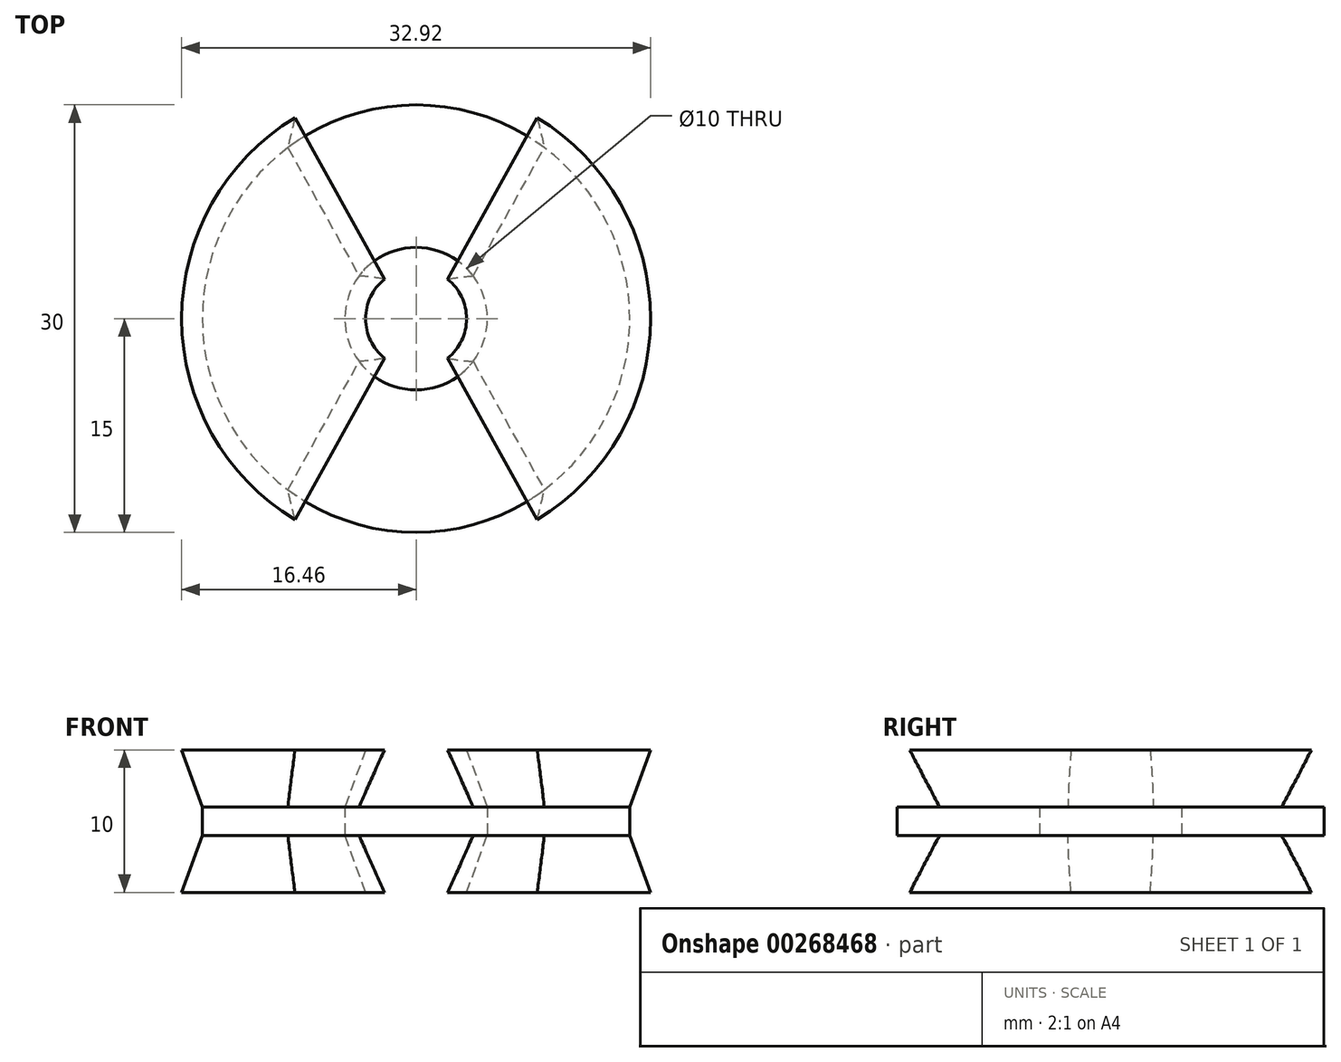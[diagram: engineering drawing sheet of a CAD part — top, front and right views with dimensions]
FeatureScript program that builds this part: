
annotation { "Feature Type Name" : "Feature", "Feature Type Description" : "" }
export const myFeature = defineFeature(function(context is Context, id is Id, definition is map)
    precondition{}
    {
        {
            var Q0;
            Q0=qCreatedBy(makeId("Top.planeOp"),FACE);
            var sketch = newSketch(context, id + "F0", { "sketchPlane" : qUnion([Q0])});
            skCircle(sketch, "E0", {"center": v(0, 0) * mm, "radius": 15 * mm});
            skCircle(sketch, "E1", {"center": v(0, 0) * mm, "radius": 5 * mm});
            skSolve(sketch);
        }
        {
            var Q0;
            Q0=makeQuery(id+"F0.imprint","IMPRINT",FACE,{"disambiguationData":[TD([[makeQuery(id+"F0.imprint","IMPRINT",EDGE,{"derivedFrom":sQuery(id+"F0.wireOp",EDGE,"E0")}),1.0]])]});
            extrude(context, id + "F1", {"entities" : qUnion([Q0]), "depth" : 2 * mm});
        }
        {
            var Q0;
            Q0=makeQuery(id+"F1.opExtrude","CAP_FACE",FACE,{"disambiguationData":[OSD([sQuery(id+"F0.wireOp",EDGE,"E0"),sQuery(id+"F0.wireOp",EDGE,"E1")])],"isStart":false});
            var sketch = newSketch(context, id + "F2", { "sketchPlane" : qUnion([Q0])});
            skLineSegment(sketch, "E2", {"start": v(-4, 3) * mm, "end": v(-9, 12) * mm});
            skLineSegment(sketch, "E3", {"start": v(4, 3) * mm, "end": v(9, 12) * mm});
            skLineSegment(sketch, "E4", {"start": v(4, -3) * mm, "end": v(9, -12) * mm});
            skLineSegment(sketch, "E5", {"start": v(-4, -3) * mm, "end": v(-9, -12) * mm});
            skSolve(sketch);
        }
        {
            var Q0;
            {var subQ0=sQuery(id+"F2.wireOp",EDGE,"E2");Q0=makeQuery(id+"F2.imprint","IMPRINT",FACE,{"disambiguationData":[TD([[makeQuery(id+"F2.imprint","IMPRINT",EDGE,{"derivedFrom":subQ0}),1.0]])]});}
            var Q1;
            {var subQ0=sQuery(id+"F2.wireOp",EDGE,"E3");Q1=makeQuery(id+"F2.imprint","IMPRINT",FACE,{"disambiguationData":[TD([[makeQuery(id+"F2.imprint","IMPRINT",EDGE,{"derivedFrom":subQ0}),-1.0]])]});}
            extrude(context, id + "F3", {"entities" : qUnion([Q0, Q1]), "operationType" : NewBodyOperationType.ADD, "depth" : 4 * mm, "hasDraft" : true, "draftAngle" : 20 * degree});
        }
        {
            var Q0;
            Q0=makeQuery(id+"F1.opExtrude","CAP_FACE",FACE,{"disambiguationData":[OSD([sQuery(id+"F0.wireOp",EDGE,"E0"),sQuery(id+"F0.wireOp",EDGE,"E1")])],"isStart":true});
            var sketch = newSketch(context, id + "F4", { "sketchPlane" : qUnion([Q0])});
            skLineSegment(sketch, "E6", {"start": v(-4, 3) * mm, "end": v(-9, 12) * mm});
            skLineSegment(sketch, "E7", {"start": v(4, 3) * mm, "end": v(9, 12) * mm});
            skLineSegment(sketch, "E8", {"start": v(9, -12) * mm, "end": v(4, -3) * mm});
            skLineSegment(sketch, "E9", {"start": v(-4, -3) * mm, "end": v(-9, -12) * mm});
            skSolve(sketch);
        }
        {
            var Q0;
            {var subQ0=sQuery(id+"F4.wireOp",EDGE,"E6");Q0=makeQuery(id+"F4.imprint","IMPRINT",FACE,{"disambiguationData":[TD([[makeQuery(id+"F4.imprint","IMPRINT",EDGE,{"derivedFrom":subQ0}),1.0]])]});}
            var Q1;
            {var subQ0=sQuery(id+"F4.wireOp",EDGE,"E7");Q1=makeQuery(id+"F4.imprint","IMPRINT",FACE,{"disambiguationData":[TD([[makeQuery(id+"F4.imprint","IMPRINT",EDGE,{"derivedFrom":subQ0}),-1.0]])]});}
            extrude(context, id + "F5", {"entities" : qUnion([Q0, Q1]), "operationType" : NewBodyOperationType.ADD, "depth" : 4 * mm, "hasDraft" : true, "draftAngle" : 20 * degree});
        }
    });
